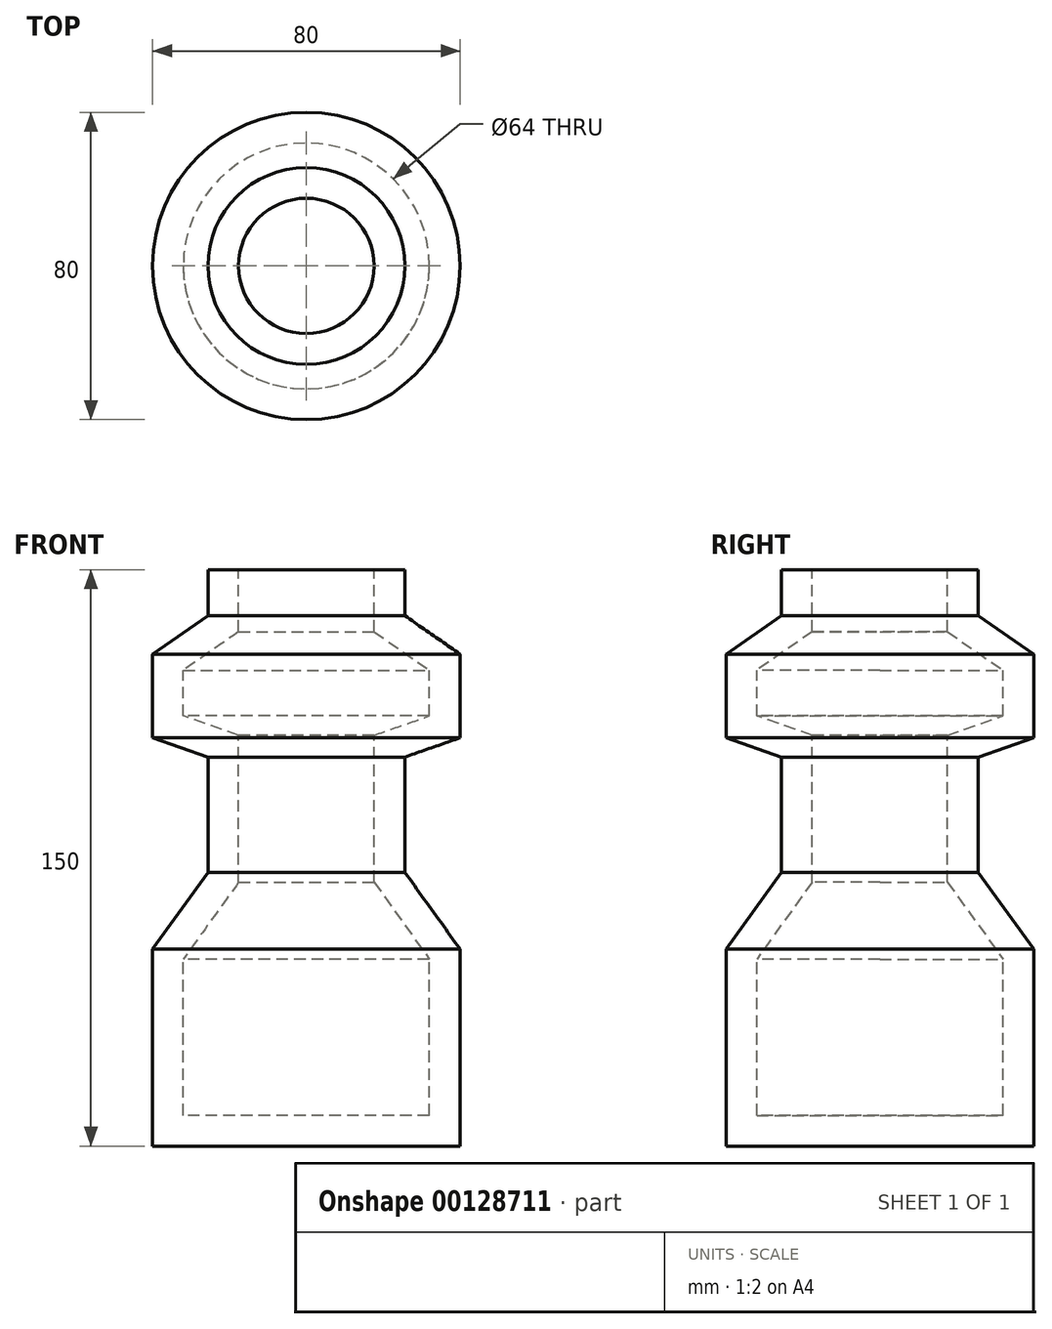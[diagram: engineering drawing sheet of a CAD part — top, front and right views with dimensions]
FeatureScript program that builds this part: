
annotation { "Feature Type Name" : "Feature", "Feature Type Description" : "" }
export const myFeature = defineFeature(function(context is Context, id is Id, definition is map)
    precondition{}
    {
        {
            var Q0;
            Q0=qCreatedBy(makeId("Front.planeOp"),FACE);
            var sketch = newSketch(context, id + "F0", { "sketchPlane" : qUnion([Q0])});
            skLineSegment(sketch, "E0", {"start": v(0, 0) * mm, "end": v(40, 0) * mm});
            skLineSegment(sketch, "E1", {"start": v(40, 51.23) * mm, "end": v(40, 0) * mm});
            skLineSegment(sketch, "E2", {"start": v(40, 51.23) * mm, "end": v(25.6, 71.23) * mm});
            skLineSegment(sketch, "E3", {"start": v(25.6, 71.23) * mm, "end": v(25.6, 101.23) * mm});
            skLineSegment(sketch, "E4", {"start": v(25.6, 101.23) * mm, "end": v(40, 106.23) * mm});
            skLineSegment(sketch, "E5", {"start": v(40, 106.23) * mm, "end": v(40, 128) * mm});
            skLineSegment(sketch, "E6", {"start": v(40, 128) * mm, "end": v(25.6, 138) * mm});
            skLineSegment(sketch, "E7", {"start": v(25.6, 138) * mm, "end": v(25.6, 150) * mm});
            skLineSegment(sketch, "E8", {"start": v(25.6, 150) * mm, "end": v(0, 150) * mm});
            skLineSegment(sketch, "E9", {"start": v(0, 150) * mm, "end": v(0, 0) * mm});
            skSolve(sketch);
        }
        {
            var Q0;
            Q0=makeQuery(id+"F0.imprint","IMPRINT",FACE,{"disambiguationData":[TD([[makeQuery(id+"F0.imprint","IMPRINT",EDGE,{"derivedFrom":sQuery(id+"F0.wireOp",EDGE,"E0")}),1.0]])]});
            var Q1;
            Q1=sQuery(id+"F0.wireOp",EDGE,"E9");
            revolve(context, id + "F1", {"entities" : qUnion([Q0]), "axis" : qUnion([Q1]), "revolveType" : RevolveType.FULL});
        }
        {
            var Q0;
            Q0=makeQuery(id+"F1.opRevolve","SWEPT_FACE",FACE,{"disambiguationData":[OSD([sQuery(id+"F0.wireOp",EDGE,"E8")])]});
            shell(context, id + "F2", {"entities" : qUnion([Q0]), "thickness" : 8 * mm});
        }
    });
